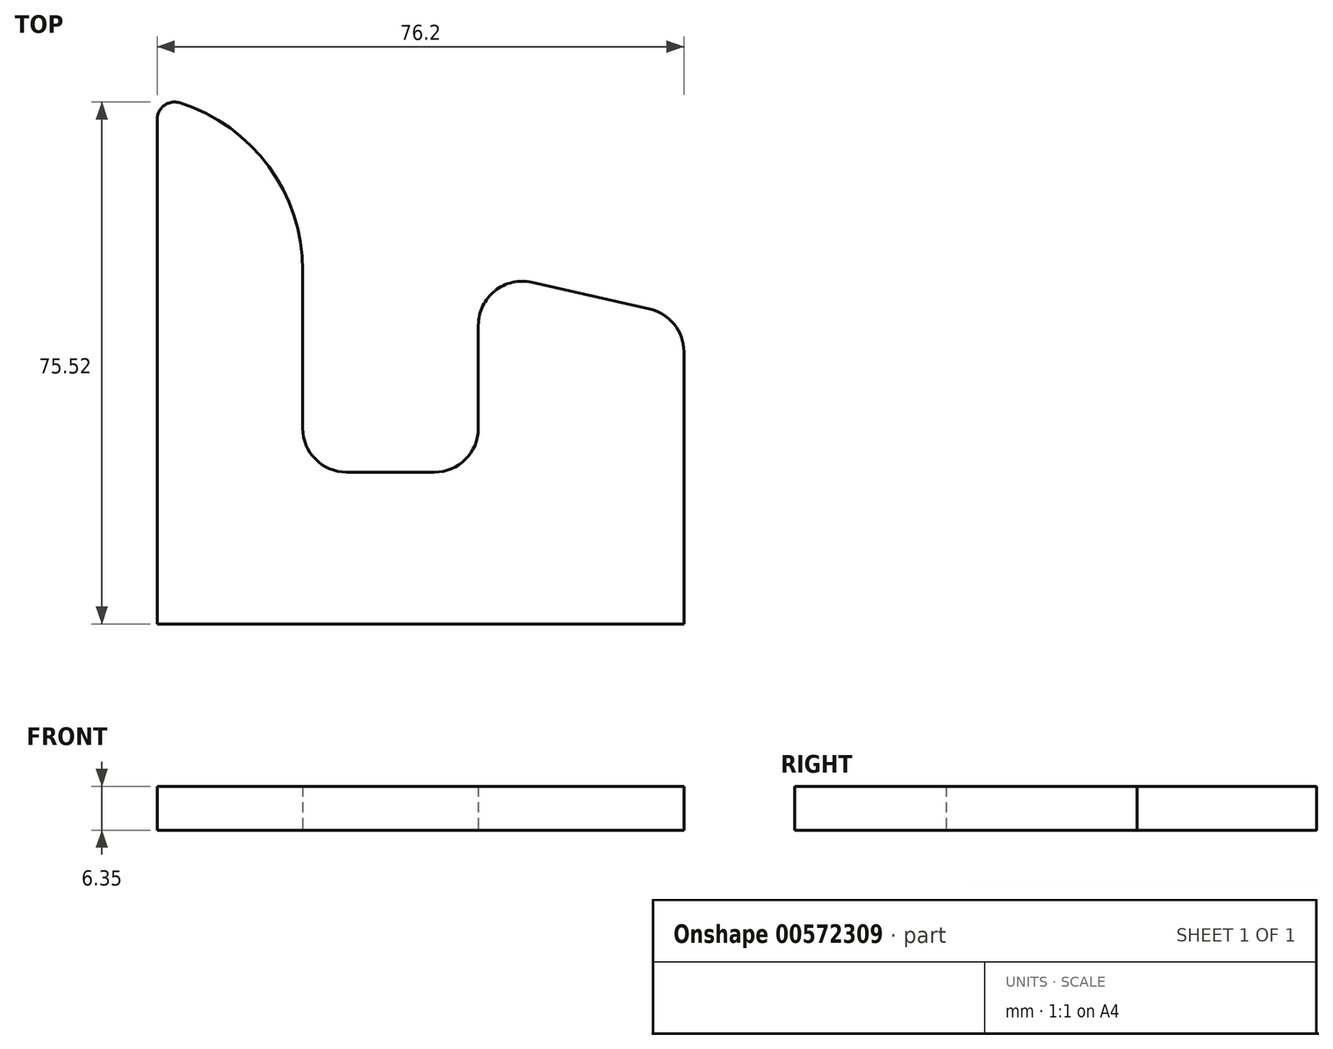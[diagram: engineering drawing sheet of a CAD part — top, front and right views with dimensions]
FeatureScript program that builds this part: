
annotation { "Feature Type Name" : "Feature", "Feature Type Description" : "" }
export const myFeature = defineFeature(function(context is Context, id is Id, definition is map)
    precondition{}
    {
        {
            var Q0;
            Q0=qCreatedBy(makeId("Top.planeOp"),FACE);
            var sketch = newSketch(context, id + "F0", { "sketchPlane" : qUnion([Q0])});
            skLineSegment(sketch, "E0", {"start": v(40.59, -38.22) * mm, "end": v(-35.61, -38.22) * mm});
            skLineSegment(sketch, "E1", {"start": v(-35.61, -38.22) * mm, "end": v(-35.61, 34.76) * mm});
            skLineSegment(sketch, "E2", {"start": v(40.59, -38.22) * mm, "end": v(40.59, 1.16) * mm});
            skLineSegment(sketch, "E3", {"start": v(35.64, 7.35) * mm, "end": v(18.6, 11.2) * mm});
            skLineSegment(sketch, "E4", {"start": v(10.86, 5) * mm, "end": v(10.86, -9.9) * mm});
            skLineSegment(sketch, "E5", {"start": v(4.5, -16.26) * mm, "end": v(-8.2, -16.26) * mm});
            skLineSegment(sketch, "E6", {"start": v(-14.54, -9.9) * mm, "end": v(-14.54, 12.95) * mm});
            skArc(sketch, "E7", {"start": v(-14.54, 12.95) * mm, "mid": v(-19.46, 27.97) * mm, "end": v(-32.3, 37.18) * mm});
            skPoint(sketch, "E8.visualSharp", {"position": v(40.59, 6.23) * mm});
            skArc(sketch, "E8.filletArc", {"start": v(40.59, 1.16) * mm, "mid": v(39.2, 5.12) * mm, "end": v(35.64, 7.35) * mm});
            skPoint(sketch, "E9.visualSharp", {"position": v(10.86, 12.95) * mm});
            skArc(sketch, "E9.filletArc", {"start": v(18.6, 11.2) * mm, "mid": v(13.24, 9.97) * mm, "end": v(10.86, 5) * mm});
            skPoint(sketch, "E10.visualSharp", {"position": v(-35.61, 37.98) * mm});
            skArc(sketch, "E10.filletArc", {"start": v(-32.3, 37.18) * mm, "mid": v(-34.57, 36.8) * mm, "end": v(-35.61, 34.76) * mm});
            skPoint(sketch, "E11.visualSharp", {"position": v(-14.54, -16.26) * mm});
            skArc(sketch, "E11.filletArc", {"start": v(-14.54, -9.9) * mm, "mid": v(-12.68, -14.4) * mm, "end": v(-8.2, -16.26) * mm});
            skPoint(sketch, "E12.visualSharp", {"position": v(10.86, -16.26) * mm});
            skArc(sketch, "E12.filletArc", {"start": v(4.5, -16.26) * mm, "mid": v(9, -14.4) * mm, "end": v(10.86, -9.9) * mm});
            skSolve(sketch);
        }
        {
            var Q0;
            Q0=makeQuery(id+"F0.imprint","IMPRINT",FACE,{"disambiguationData":[TD([[makeQuery(id+"F0.imprint","IMPRINT",EDGE,{"derivedFrom":sQuery(id+"F0.wireOp",EDGE,"E0")}),-1.0]])]});
            extrude(context, id + "F1", {"entities" : qUnion([Q0]), "depth" : 6.35 * mm, "offsetDistance" : 25.4 * mm});
        }
    });
